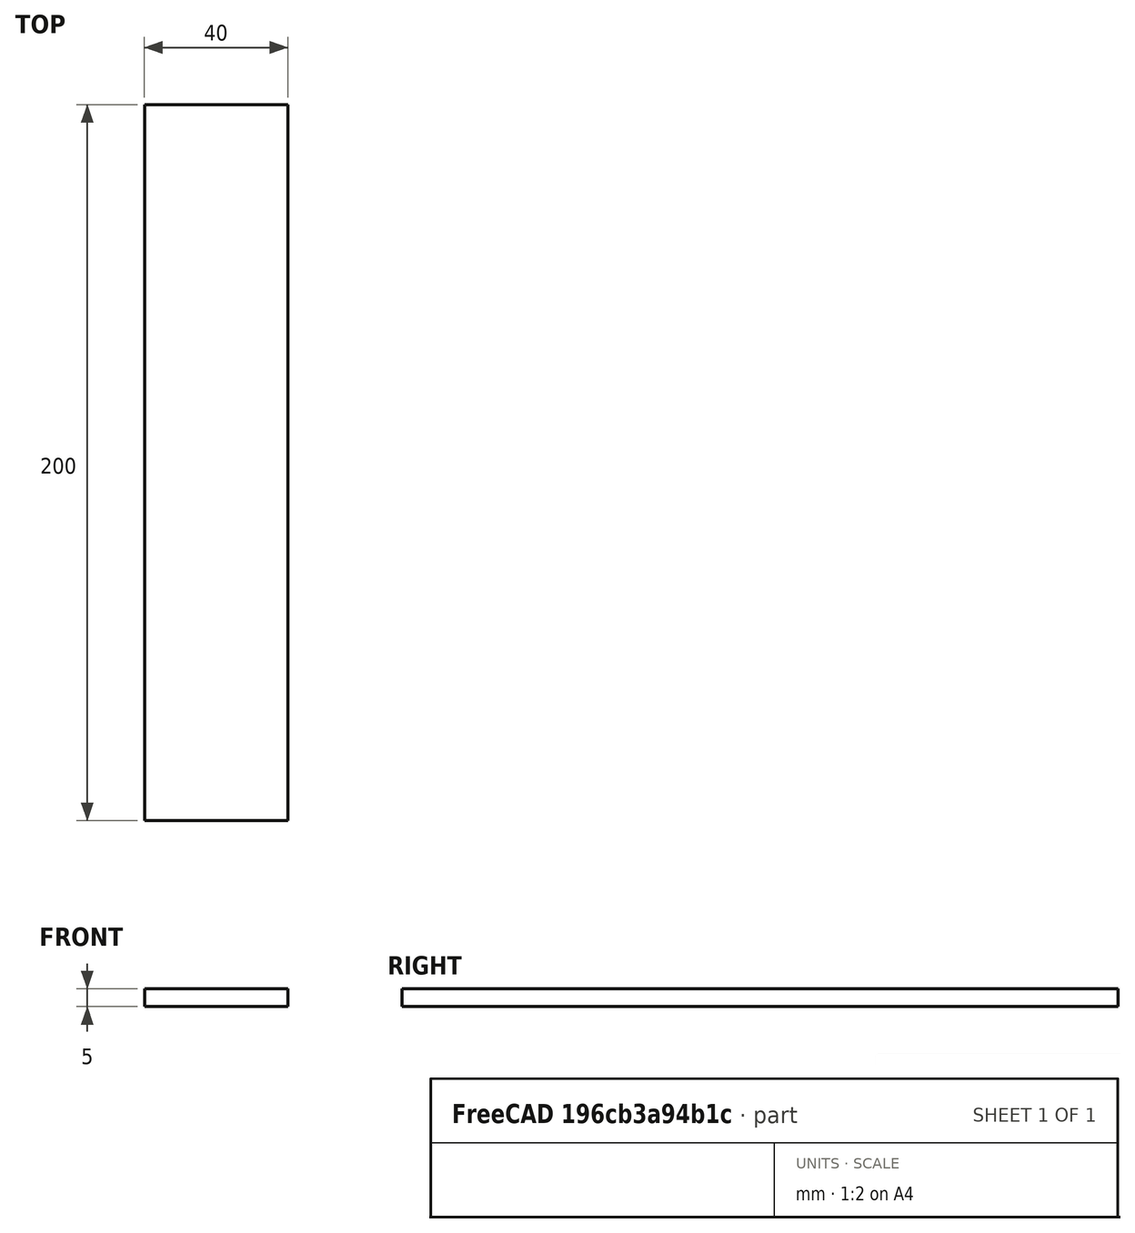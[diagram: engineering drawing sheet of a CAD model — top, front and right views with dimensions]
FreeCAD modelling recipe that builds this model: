
FCSTD DOCUMENT  (FreeCAD 0.17R13541 (Git))
Label: 40x200x5rectangle
License: All rights reserved
LicenseURL: http://en.wikipedia.org/wiki/All_rights_reserved
objects: Sketcher::SketchObject×1, Part::Extrusion×1
note: 2 computed .brp shape members not serialized (recipe doc carries the construction recipe); baked Part::Feature solids carry a one-line shape summary decoded from their .brp

FEATURE [Sketcher::SketchObject] Sketch
  sketch-geometry (4):
    g0: LineSegment StartX=-17.3951 StartY=71.6154 StartZ=0 EndX=22.6049 EndY=71.6154 EndZ=0
    g1: LineSegment StartX=22.6049 StartY=71.6154 StartZ=0 EndX=22.6049 EndY=-128.385 EndZ=0
    g2: LineSegment StartX=22.6049 StartY=-128.385 StartZ=0 EndX=-17.3951 EndY=-128.385 EndZ=0
    g3: LineSegment StartX=-17.3951 StartY=-128.385 StartZ=0 EndX=-17.3951 EndY=71.6154 EndZ=0
  constraints (12):
    c: Coincident(g0,g1)
    c: Coincident(g1,g2)
    c: Coincident(g2,g3)
    c: Coincident(g3,g0)
    c: Horizontal(g0)
    c: Horizontal(g2)
    c: Vertical(g1)
    c: Vertical(g3)
    c: Equal(g0,g2)
    c: Equal(g1,g3)
    c: Distance(g1) = 200
    c: Distance(g0) = 40
FEATURE [Part::Extrusion] Extrude
  Base = -> Sketch
  Dir = (0,0,1)
  DirMode = 2
  FaceMakerClass = Part::FaceMakerBullseye
  LengthFwd = 5
  LengthRev = 0
  Solid = true
  Symmetric = false
